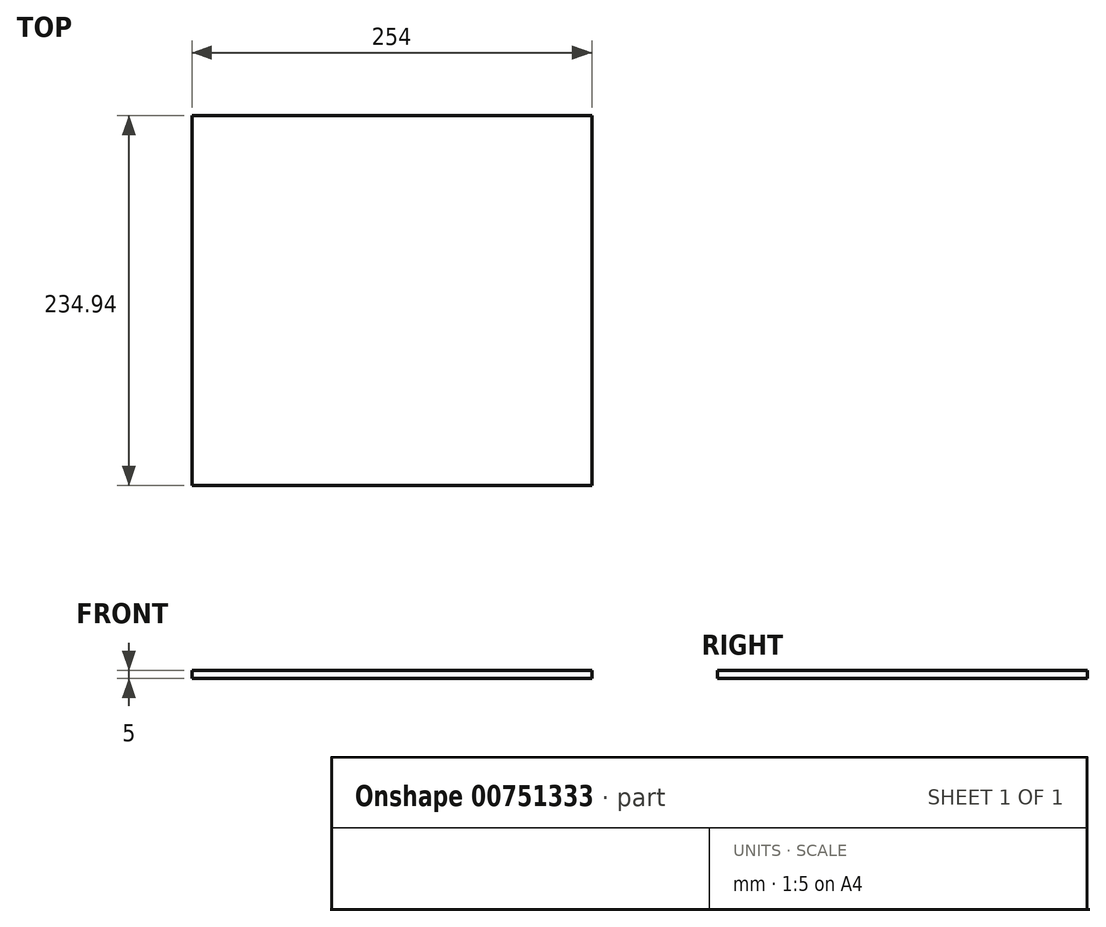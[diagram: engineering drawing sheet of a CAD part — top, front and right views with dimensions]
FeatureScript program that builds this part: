
annotation { "Feature Type Name" : "Feature", "Feature Type Description" : "" }
export const myFeature = defineFeature(function(context is Context, id is Id, definition is map)
    precondition{}
    {
        {
            var Q0;
            Q0=qCreatedBy(makeId("Top.planeOp"),FACE);
            var sketch = newSketch(context, id + "F0", { "sketchPlane" : qUnion([Q0])});
            skLineSegment(sketch, "E0.bottom", {"start": v(127, 117.48) * mm, "end": v(-127, 117.48) * mm});
            skLineSegment(sketch, "E0.top", {"start": v(127, -117.48) * mm, "end": v(-127, -117.48) * mm});
            skLineSegment(sketch, "E0.left", {"start": v(127, 117.48) * mm, "end": v(127, -117.48) * mm});
            skLineSegment(sketch, "E0.right", {"start": v(-127, 117.48) * mm, "end": v(-127, -117.48) * mm});
            skPoint(sketch, "E0.middle", {"position": v(0, 0) * mm});
            skSolve(sketch);
        }
        {
            var Q0;
            Q0 = qSketchRegion(id + "F0", true);
            extrude(context, id + "F1", {"entities" : qUnion([Q0]), "depth" : 5 * mm, "offsetDistance" : 25 * mm});
        }
    });
